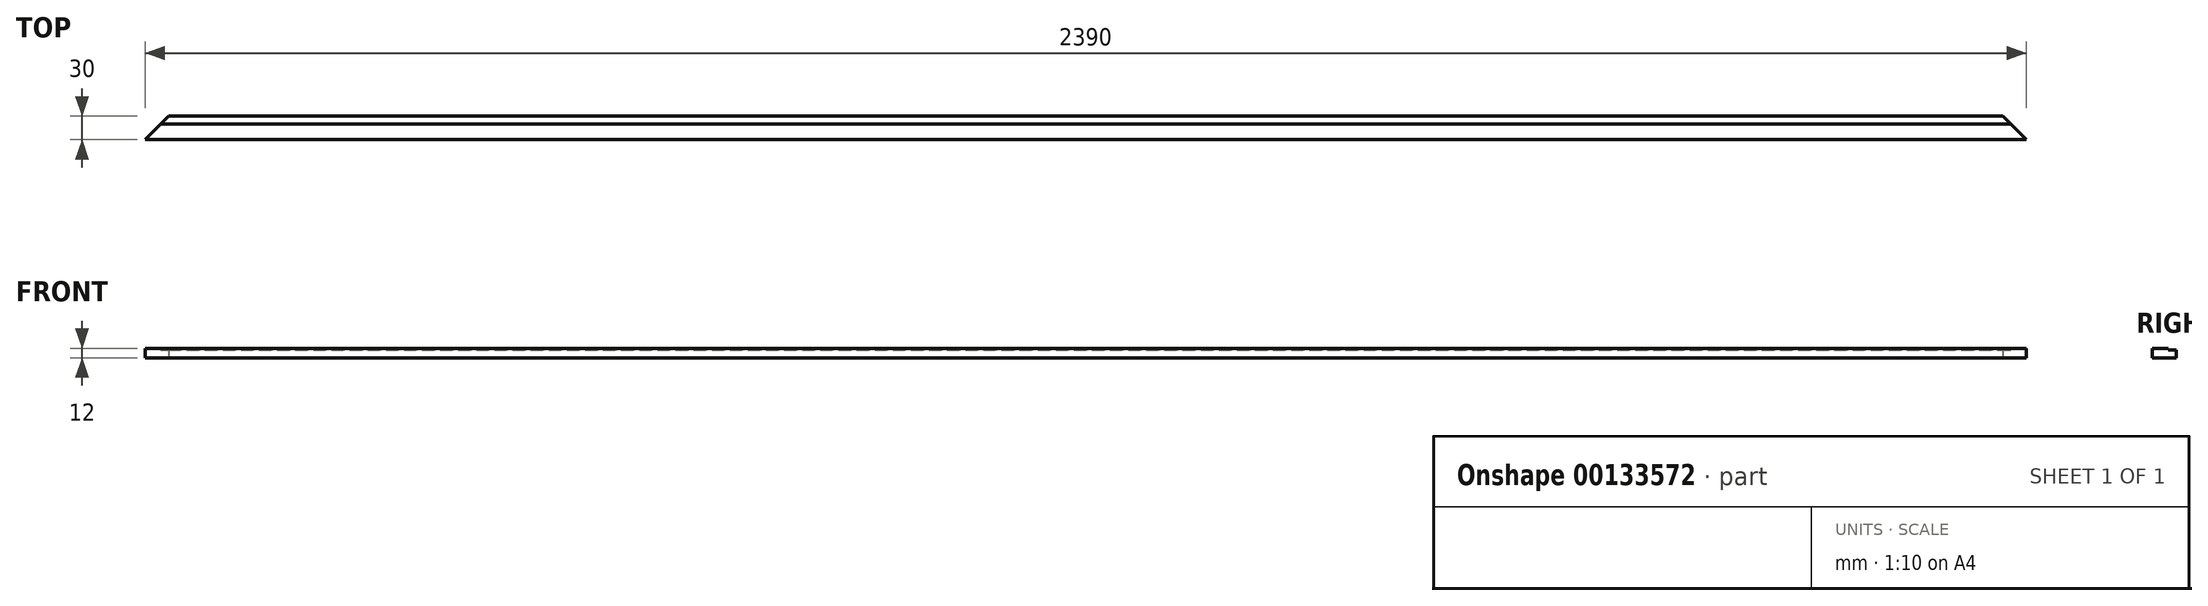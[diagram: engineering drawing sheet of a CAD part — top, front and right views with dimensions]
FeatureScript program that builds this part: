
annotation { "Feature Type Name" : "Feature", "Feature Type Description" : "" }
export const myFeature = defineFeature(function(context is Context, id is Id, definition is map)
    precondition{}
    {
        {
            var Q0;
            Q0=qCreatedBy(makeId("Top.planeOp"),FACE);
            var sketch = newSketch(context, id + "F0", { "sketchPlane" : qUnion([Q0])});
            skLineSegment(sketch, "E0", {"start": v(0, 0) * mm, "end": v(2390, 0) * mm});
            skLineSegment(sketch, "E1", {"start": v(2390, 0) * mm, "end": v(2370, 20) * mm});
            skLineSegment(sketch, "E2", {"start": v(2370, 20) * mm, "end": v(20, 20) * mm});
            skLineSegment(sketch, "E3", {"start": v(20, 20) * mm, "end": v(0, 0) * mm});
            skLineSegment(sketch, "E4", {"start": v(20, 20) * mm, "end": v(30, 30) * mm});
            skLineSegment(sketch, "E5", {"start": v(30, 30) * mm, "end": v(2360, 30) * mm});
            skLineSegment(sketch, "E6", {"start": v(2360, 30) * mm, "end": v(2370, 20) * mm});
            skSolve(sketch);
        }
        {
            var Q0;
            Q0=makeQuery(id+"F0.imprint","IMPRINT",FACE,{"disambiguationData":[TD([[makeQuery(id+"F0.imprint","IMPRINT",EDGE,{"derivedFrom":sQuery(id+"F0.wireOp",EDGE,"E0")}),1.0]])]});
            extrude(context, id + "F1", {"entities" : qUnion([Q0]), "depth" : 12 * mm});
        }
        {
            var Q0;
            Q0=makeQuery(id+"F0.imprint","IMPRINT",FACE,{"disambiguationData":[TD([[makeQuery(id+"F0.imprint","IMPRINT",EDGE,{"derivedFrom":sQuery(id+"F0.wireOp",EDGE,"E2")}),-1.0]])]});
            extrude(context, id + "F2", {"entities" : qUnion([Q0]), "operationType" : NewBodyOperationType.ADD, "depth" : 10 * mm});
        }
        {
            var Q0;
            Q0=makeQuery(id+"F1.opExtrude","SWEPT_BODY",BODY,{"disambiguationData":[OSD([sQuery(id+"F0.wireOp",EDGE,"E0"),sQuery(id+"F0.wireOp",EDGE,"E1"),sQuery(id+"F0.wireOp",EDGE,"E2"),sQuery(id+"F0.wireOp",EDGE,"E3")])]});
            transform(context, id + "F3", {"entities" : qUnion([Q0]), "transformType" : TransformType.TRANSLATION_3D, "dx" : 0 * mm, "dy" : 0 * mm, "dz" : 0 * mm, "makeCopy" : true});
        }
        {
            var Q0;
            Q0=makeQuery(id+"F3.opPattern","COPY",BODY,{"derivedFrom":makeQuery(id+"F1.opExtrude","SWEPT_BODY",BODY,{"disambiguationData":[OSD([sQuery(id+"F0.wireOp",EDGE,"E0"),sQuery(id+"F0.wireOp",EDGE,"E1"),sQuery(id+"F0.wireOp",EDGE,"E2"),sQuery(id+"F0.wireOp",EDGE,"E3")])]}),"instanceName":"1"});
            deleteBodies(context, id + "F4", {"entities" : qUnion([Q0])});
        }
    });
